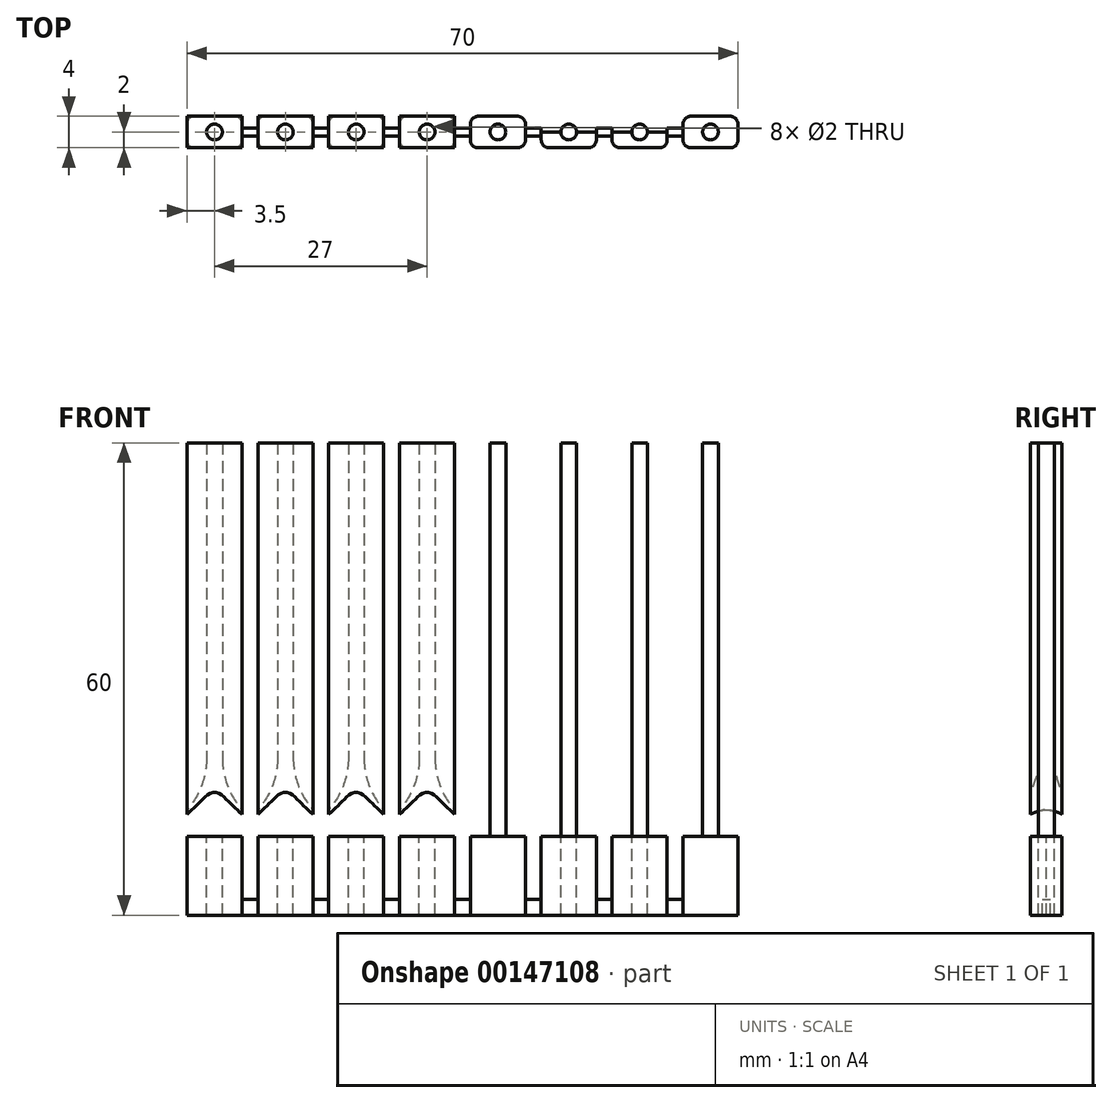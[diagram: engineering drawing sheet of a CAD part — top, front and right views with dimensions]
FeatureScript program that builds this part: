
annotation { "Feature Type Name" : "Feature", "Feature Type Description" : "" }
export const myFeature = defineFeature(function(context is Context, id is Id, definition is map)
    precondition{}
    {
        {
            var Q0;
            Q0=qCreatedBy(makeId("Top.planeOp"),FACE);
            var sketch = newSketch(context, id + "F0", { "sketchPlane" : qUnion([Q0])});
            skLineSegment(sketch, "E0.bottom", {"start": v(35, 2) * mm, "end": v(-35, 2) * mm});
            skLineSegment(sketch, "E0.top", {"start": v(35, -2) * mm, "end": v(-35, -2) * mm});
            skLineSegment(sketch, "E0.left", {"start": v(35, 2) * mm, "end": v(35, -2) * mm});
            skLineSegment(sketch, "E0.right", {"start": v(-35, 2) * mm, "end": v(-35, -2) * mm});
            skPoint(sketch, "E0.middle", {"position": v(0, 0) * mm});
            skLineSegment(sketch, "E1", {"start": v(0, 0) * mm, "end": v(4.5, 0) * mm});
            skLineSegment(sketch, "E2", {"start": v(4.5, 0) * mm, "end": v(13.5, 0) * mm});
            skLineSegment(sketch, "E3", {"start": v(13.5, 0) * mm, "end": v(22.5, 0) * mm});
            skLineSegment(sketch, "E4", {"start": v(22.5, 0) * mm, "end": v(31.5, 0) * mm});
            skCircle(sketch, "E5", {"center": v(4.5, 0) * mm, "radius": 1 * mm});
            skCircle(sketch, "E6", {"center": v(13.5, 0) * mm, "radius": 1 * mm});
            skCircle(sketch, "E7", {"center": v(22.5, 0) * mm, "radius": 1 * mm});
            skCircle(sketch, "E8", {"center": v(31.5, 0) * mm, "radius": 1 * mm});
            skLineSegment(sketch, "E9", {"start": v(0, 2) * mm, "end": v(8, 2) * mm});
            skLineSegment(sketch, "E10", {"start": v(8, 2) * mm, "end": v(10, 2) * mm});
            skLineSegment(sketch, "E11", {"start": v(10, 2) * mm, "end": v(17, 2) * mm});
            skLineSegment(sketch, "E12", {"start": v(17, 2) * mm, "end": v(19, 2) * mm});
            skLineSegment(sketch, "E13", {"start": v(19, 2) * mm, "end": v(26, 2) * mm});
            skLineSegment(sketch, "E14", {"start": v(26, 2) * mm, "end": v(28, 2) * mm});
            skLineSegment(sketch, "E15", {"start": v(8, 2) * mm, "end": v(8, 0.5) * mm});
            skLineSegment(sketch, "E16", {"start": v(8, 0.5) * mm, "end": v(10, 0.5) * mm});
            skLineSegment(sketch, "E17", {"start": v(10, 0.5) * mm, "end": v(10, 2) * mm});
            skLineSegment(sketch, "E18", {"start": v(17, 2) * mm, "end": v(17, 0.5) * mm});
            skLineSegment(sketch, "E19", {"start": v(17, 0.5) * mm, "end": v(19, 0.5) * mm});
            skLineSegment(sketch, "E20", {"start": v(19, 0.5) * mm, "end": v(19, 2) * mm});
            skLineSegment(sketch, "E21", {"start": v(26, 2) * mm, "end": v(26, 0.5) * mm});
            skLineSegment(sketch, "E22", {"start": v(26, 0.5) * mm, "end": v(28, 0.5) * mm});
            skLineSegment(sketch, "E23", {"start": v(28, 0.5) * mm, "end": v(28, 2) * mm});
            skLineSegment(sketch, "E24.MirrorCS", {"start": v(8, -0.5) * mm, "end": v(10, -0.5) * mm});
            skLineSegment(sketch, "E25.MirrorCS", {"start": v(8, -2) * mm, "end": v(8, -0.5) * mm});
            skLineSegment(sketch, "E26.MirrorCS", {"start": v(10, -0.5) * mm, "end": v(10, -2) * mm});
            skLineSegment(sketch, "E27.MirrorCS", {"start": v(17, -2) * mm, "end": v(17, -0.5) * mm});
            skLineSegment(sketch, "E28.MirrorCS", {"start": v(19, -0.5) * mm, "end": v(19, -2) * mm});
            skLineSegment(sketch, "E29.MirrorCS", {"start": v(17, -0.5) * mm, "end": v(19, -0.5) * mm});
            skLineSegment(sketch, "E30.MirrorCS", {"start": v(26, -0.5) * mm, "end": v(28, -0.5) * mm});
            skLineSegment(sketch, "E31.MirrorCS", {"start": v(28, -0.5) * mm, "end": v(28, -2) * mm});
            skLineSegment(sketch, "E32.MirrorCS", {"start": v(26, -2) * mm, "end": v(26, -0.5) * mm});
            skLineSegment(sketch, "E33", {"start": v(10, -0.5) * mm, "end": v(10, 0.5) * mm});
            skLineSegment(sketch, "E34", {"start": v(8, -0.5) * mm, "end": v(8, 0.5) * mm});
            skLineSegment(sketch, "E35", {"start": v(17, -0.5) * mm, "end": v(17, 0.5) * mm});
            skLineSegment(sketch, "E36", {"start": v(19, -0.5) * mm, "end": v(19, 0.5) * mm});
            skLineSegment(sketch, "E37", {"start": v(26, -0.5) * mm, "end": v(26, 0.5) * mm});
            skLineSegment(sketch, "E38", {"start": v(28, -0.5) * mm, "end": v(28, 0.5) * mm});
            skLineSegment(sketch, "E39.MirrorCS", {"start": v(-8, -2) * mm, "end": v(-8, -0.5) * mm});
            skCircle(sketch, "E40.MirrorC", {"center": v(-4.5, 0) * mm, "radius": 1 * mm});
            skLineSegment(sketch, "E41.MirrorCS", {"start": v(-8, 2) * mm, "end": v(-8, 0.5) * mm});
            skLineSegment(sketch, "E42.MirrorCS", {"start": v(-8, 0.5) * mm, "end": v(-10, 0.5) * mm});
            skLineSegment(sketch, "E43.MirrorCS", {"start": v(-10, -0.5) * mm, "end": v(-10, -2) * mm});
            skCircle(sketch, "E44.MirrorC", {"center": v(-13.5, 0) * mm, "radius": 1 * mm});
            skLineSegment(sketch, "E45.MirrorCS", {"start": v(-17, -2) * mm, "end": v(-17, -0.5) * mm});
            skLineSegment(sketch, "E46.MirrorCS", {"start": v(-19, -0.5) * mm, "end": v(-19, -2) * mm});
            skLineSegment(sketch, "E47.MirrorCS", {"start": v(-17, -0.5) * mm, "end": v(-19, -0.5) * mm});
            skLineSegment(sketch, "E48.MirrorCS", {"start": v(-17, 0.5) * mm, "end": v(-19, 0.5) * mm});
            skLineSegment(sketch, "E49.MirrorCS", {"start": v(-19, 0.5) * mm, "end": v(-19, 2) * mm});
            skLineSegment(sketch, "E50.MirrorCS", {"start": v(-17, 2) * mm, "end": v(-17, 0.5) * mm});
            skCircle(sketch, "E51.MirrorC", {"center": v(-22.5, 0) * mm, "radius": 1 * mm});
            skLineSegment(sketch, "E52.MirrorCS", {"start": v(-26, -2) * mm, "end": v(-26, -0.5) * mm});
            skLineSegment(sketch, "E53.MirrorCS", {"start": v(-28, -0.5) * mm, "end": v(-28, -2) * mm});
            skLineSegment(sketch, "E54.MirrorCS", {"start": v(-26, -0.5) * mm, "end": v(-28, -0.5) * mm});
            skLineSegment(sketch, "E55.MirrorCS", {"start": v(-26, 0.5) * mm, "end": v(-28, 0.5) * mm});
            skLineSegment(sketch, "E56.MirrorCS", {"start": v(-28, 0.5) * mm, "end": v(-28, 2) * mm});
            skLineSegment(sketch, "E57.MirrorCS", {"start": v(-26, 2) * mm, "end": v(-26, 0.5) * mm});
            skCircle(sketch, "E58.MirrorC", {"center": v(-31.5, 0) * mm, "radius": 1 * mm});
            skLineSegment(sketch, "E59.MirrorCS", {"start": v(-28, -0.5) * mm, "end": v(-28, 0.5) * mm});
            skLineSegment(sketch, "E60.MirrorCS", {"start": v(-26, -0.5) * mm, "end": v(-26, 0.5) * mm});
            skLineSegment(sketch, "E61.MirrorCS", {"start": v(-19, -0.5) * mm, "end": v(-19, 0.5) * mm});
            skLineSegment(sketch, "E62.MirrorCS", {"start": v(-17, -0.5) * mm, "end": v(-17, 0.5) * mm});
            skLineSegment(sketch, "E63.MirrorCS", {"start": v(-8, -0.5) * mm, "end": v(-8, 0.5) * mm});
            skLineSegment(sketch, "E64.MirrorCS", {"start": v(-10, -0.5) * mm, "end": v(-10, 0.5) * mm});
            skLineSegment(sketch, "E65.MirrorCS", {"start": v(-8, -0.5) * mm, "end": v(-10, -0.5) * mm});
            skLineSegment(sketch, "E66.MirrorCS", {"start": v(-10, 0.5) * mm, "end": v(-10, 2) * mm});
            skLineSegment(sketch, "E67", {"start": v(8, 2) * mm, "end": v(1, 2) * mm});
            skLineSegment(sketch, "E68", {"start": v(1, 2) * mm, "end": v(1, 0.5) * mm});
            skLineSegment(sketch, "E69", {"start": v(1, 0.5) * mm, "end": v(-1, 0.5) * mm});
            skLineSegment(sketch, "E70", {"start": v(-1, 0.5) * mm, "end": v(-1, 2) * mm});
            skLineSegment(sketch, "E71", {"start": v(8, -2) * mm, "end": v(1, -2) * mm});
            skLineSegment(sketch, "E72", {"start": v(1, -2) * mm, "end": v(1, -0.5) * mm});
            skLineSegment(sketch, "E73", {"start": v(1, -0.5) * mm, "end": v(-1, -0.5) * mm});
            skLineSegment(sketch, "E74", {"start": v(-1, -0.5) * mm, "end": v(-1, -2) * mm});
            skLineSegment(sketch, "E75", {"start": v(1, -0.5) * mm, "end": v(1, 0.5) * mm});
            skLineSegment(sketch, "E76", {"start": v(-1, -0.5) * mm, "end": v(-1, 0.5) * mm});
            skSolve(sketch);
        }
        {
            var Q0;
            {var subQ0=sQuery(id+"F0.wireOp",EDGE,"E0.left");Q0=makeQuery(id+"F0.imprint","IMPRINT",FACE,{"disambiguationData":[TD([[makeQuery(id+"F0.imprint","IMPRINT",EDGE,{"derivedFrom":subQ0}),-1.0]])]});}
            var Q1;
            {var subQ6=sQuery(id+"F0.wireOp",EDGE,"E0.right");Q1=makeQuery(id+"F0.imprint","IMPRINT",FACE,{"disambiguationData":[TD([[makeQuery(id+"F0.imprint","IMPRINT",EDGE,{"derivedFrom":subQ6}),1.0]])]});}
            var Q2;
            {var subQ10=sQuery(id+"F0.wireOp",EDGE,"E28.MirrorCS");Q2=makeQuery(id+"F0.imprint","IMPRINT",FACE,{"disambiguationData":[TD([[makeQuery(id+"F0.imprint","IMPRINT",EDGE,{"derivedFrom":subQ10}),1.0]])]});}
            var Q3;
            {var subQ5=sQuery(id+"F0.wireOp",EDGE,"E26.MirrorCS");Q3=makeQuery(id+"F0.imprint","IMPRINT",FACE,{"disambiguationData":[TD([[makeQuery(id+"F0.imprint","IMPRINT",EDGE,{"derivedFrom":subQ5}),1.0]])]});}
            var Q4;
            Q4=makeQuery(id+"F0.imprint","IMPRINT",FACE,{"disambiguationData":[TD([[makeQuery(id+"F0.imprint","IMPRINT",EDGE,{"derivedFrom":sQuery(id+"F0.wireOp",EDGE,"E11")}),-1.0]])]});
            var Q5;
            Q5=makeQuery(id+"F0.imprint","IMPRINT",FACE,{"disambiguationData":[TD([[makeQuery(id+"F0.imprint","IMPRINT",EDGE,{"derivedFrom":sQuery(id+"F0.wireOp",EDGE,"E13")}),-1.0]])]});
            var Q6;
            {var subQ1=sQuery(id+"F0.wireOp",EDGE,"E46.MirrorCS");Q6=makeQuery(id+"F0.imprint","IMPRINT",FACE,{"disambiguationData":[TD([[makeQuery(id+"F0.imprint","IMPRINT",EDGE,{"derivedFrom":subQ1}),-1.0]])]});}
            var Q7;
            {var subQ0=sQuery(id+"F0.wireOp",EDGE,"E43.MirrorCS");Q7=makeQuery(id+"F0.imprint","IMPRINT",FACE,{"disambiguationData":[TD([[makeQuery(id+"F0.imprint","IMPRINT",EDGE,{"derivedFrom":subQ0}),-1.0]])]});}
            var Q8;
            {var subQ2=sQuery(id+"F0.wireOp",EDGE,"E15");Q8=makeQuery(id+"F0.imprint","IMPRINT",FACE,{"disambiguationData":[TD([[makeQuery(id+"F0.imprint","IMPRINT",EDGE,{"derivedFrom":subQ2}),-1.0]])]});}
            var Q9;
            {var subQ0=sQuery(id+"F0.wireOp",EDGE,"E25.MirrorCS");Q9=makeQuery(id+"F0.imprint","IMPRINT",FACE,{"disambiguationData":[TD([[makeQuery(id+"F0.imprint","IMPRINT",EDGE,{"derivedFrom":subQ0}),1.0]])]});}
            var Q10;
            {var subQ0=sQuery(id+"F0.wireOp",EDGE,"E39.MirrorCS");Q10=makeQuery(id+"F0.imprint","IMPRINT",FACE,{"disambiguationData":[TD([[makeQuery(id+"F0.imprint","IMPRINT",EDGE,{"derivedFrom":subQ0}),-1.0]])]});}
            var Q11;
            Q11=makeQuery(id+"F0.imprint","IMPRINT",FACE,{"disambiguationData":[TD([[makeQuery(id+"F0.imprint","IMPRINT",EDGE,{"derivedFrom":sQuery(id+"F0.wireOp",EDGE,"E8")}),1.0]])]});
            var Q12;
            {var subQ0=sQuery(id+"F0.wireOp",EDGE,"E4");var subQ1=sQuery(id+"F0.wireOp",EDGE,"E3");var subQ2=makeQuery(id+"F0.imprint","INTERSECT",VERTEX,{"derivedFrom":[subQ1,subQ0]});Q12=makeQuery(id+"F0.imprint","IMPRINT",FACE,{"disambiguationData":[TD([[makeQuery(id+"F0.imprint","IMPRINT",EDGE,{"disambiguationData":[TD([[subQ2,1.0]])],"derivedFrom":subQ1}),1.0]])]});}
            var Q13;
            {var subQ0=sQuery(id+"F0.wireOp",EDGE,"E3");var subQ1=sQuery(id+"F0.wireOp",EDGE,"E2");var subQ2=makeQuery(id+"F0.imprint","INTERSECT",VERTEX,{"derivedFrom":[subQ1,subQ0]});Q13=makeQuery(id+"F0.imprint","IMPRINT",FACE,{"disambiguationData":[TD([[makeQuery(id+"F0.imprint","IMPRINT",EDGE,{"disambiguationData":[TD([[subQ2,1.0]])],"derivedFrom":subQ1}),1.0]])]});}
            var Q14;
            {var subQ0=sQuery(id+"F0.wireOp",EDGE,"E3");var subQ1=sQuery(id+"F0.wireOp",EDGE,"E2");var subQ2=makeQuery(id+"F0.imprint","INTERSECT",VERTEX,{"derivedFrom":[subQ1,subQ0]});Q14=makeQuery(id+"F0.imprint","IMPRINT",FACE,{"disambiguationData":[TD([[makeQuery(id+"F0.imprint","IMPRINT",EDGE,{"disambiguationData":[TD([[subQ2,1.0]])],"derivedFrom":subQ1}),-1.0]])]});}
            var Q15;
            {var subQ0=sQuery(id+"F0.wireOp",EDGE,"E4");var subQ1=sQuery(id+"F0.wireOp",EDGE,"E3");var subQ2=makeQuery(id+"F0.imprint","INTERSECT",VERTEX,{"derivedFrom":[subQ1,subQ0]});Q15=makeQuery(id+"F0.imprint","IMPRINT",FACE,{"disambiguationData":[TD([[makeQuery(id+"F0.imprint","IMPRINT",EDGE,{"disambiguationData":[TD([[subQ2,1.0]])],"derivedFrom":subQ1}),-1.0]])]});}
            var Q16;
            {var subQ0=sQuery(id+"F0.wireOp",EDGE,"E2");var subQ1=sQuery(id+"F0.wireOp",EDGE,"E1");var subQ2=makeQuery(id+"F0.imprint","INTERSECT",VERTEX,{"derivedFrom":[subQ1,subQ0]});Q16=makeQuery(id+"F0.imprint","IMPRINT",FACE,{"disambiguationData":[TD([[makeQuery(id+"F0.imprint","IMPRINT",EDGE,{"disambiguationData":[TD([[subQ2,1.0]])],"derivedFrom":subQ1}),1.0]])]});}
            var Q17;
            {var subQ0=sQuery(id+"F0.wireOp",EDGE,"E2");var subQ1=sQuery(id+"F0.wireOp",EDGE,"E1");var subQ2=makeQuery(id+"F0.imprint","INTERSECT",VERTEX,{"derivedFrom":[subQ1,subQ0]});Q17=makeQuery(id+"F0.imprint","IMPRINT",FACE,{"disambiguationData":[TD([[makeQuery(id+"F0.imprint","IMPRINT",EDGE,{"disambiguationData":[TD([[subQ2,1.0]])],"derivedFrom":subQ1}),-1.0]])]});}
            var Q18;
            Q18=makeQuery(id+"F0.imprint","IMPRINT",FACE,{"disambiguationData":[TD([[makeQuery(id+"F0.imprint","IMPRINT",EDGE,{"derivedFrom":sQuery(id+"F0.wireOp",EDGE,"E40.MirrorC")}),-1.0]])]});
            var Q19;
            Q19=makeQuery(id+"F0.imprint","IMPRINT",FACE,{"disambiguationData":[TD([[makeQuery(id+"F0.imprint","IMPRINT",EDGE,{"derivedFrom":sQuery(id+"F0.wireOp",EDGE,"E44.MirrorC")}),-1.0]])]});
            var Q20;
            Q20=makeQuery(id+"F0.imprint","IMPRINT",FACE,{"disambiguationData":[TD([[makeQuery(id+"F0.imprint","IMPRINT",EDGE,{"derivedFrom":sQuery(id+"F0.wireOp",EDGE,"E51.MirrorC")}),-1.0]])]});
            var Q21;
            Q21=makeQuery(id+"F0.imprint","IMPRINT",FACE,{"disambiguationData":[TD([[makeQuery(id+"F0.imprint","IMPRINT",EDGE,{"derivedFrom":sQuery(id+"F0.wireOp",EDGE,"E58.MirrorC")}),-1.0]])]});
            extrude(context, id + "F1", {"entities" : qUnion([Q0, Q1, Q2, Q3, Q4, Q5, Q6, Q7, Q8, Q9, Q10, Q11, Q12, Q13, Q14, Q15, Q16, Q17, Q18, Q19, Q20, Q21]), "oppositeDirection" : true, "depth" : 10 * mm});
        }
        {
            var Q0;
            {var subQ5=sQuery(id+"F0.wireOp",EDGE,"E24.MirrorCS");Q0=makeQuery(id+"F0.imprint","IMPRINT",FACE,{"disambiguationData":[TD([[makeQuery(id+"F0.imprint","IMPRINT",EDGE,{"derivedFrom":subQ5}),1.0]])]});}
            var Q1;
            {var subQ5=sQuery(id+"F0.wireOp",EDGE,"E16");Q1=makeQuery(id+"F0.imprint","IMPRINT",FACE,{"disambiguationData":[TD([[makeQuery(id+"F0.imprint","IMPRINT",EDGE,{"derivedFrom":subQ5}),-1.0]])]});}
            var Q2;
            {var subQ5=sQuery(id+"F0.wireOp",EDGE,"E29.MirrorCS");Q2=makeQuery(id+"F0.imprint","IMPRINT",FACE,{"disambiguationData":[TD([[makeQuery(id+"F0.imprint","IMPRINT",EDGE,{"derivedFrom":subQ5}),1.0]])]});}
            var Q3;
            {var subQ5=sQuery(id+"F0.wireOp",EDGE,"E19");Q3=makeQuery(id+"F0.imprint","IMPRINT",FACE,{"disambiguationData":[TD([[makeQuery(id+"F0.imprint","IMPRINT",EDGE,{"derivedFrom":subQ5}),-1.0]])]});}
            var Q4;
            {var subQ5=sQuery(id+"F0.wireOp",EDGE,"E30.MirrorCS");Q4=makeQuery(id+"F0.imprint","IMPRINT",FACE,{"disambiguationData":[TD([[makeQuery(id+"F0.imprint","IMPRINT",EDGE,{"derivedFrom":subQ5}),1.0]])]});}
            var Q5;
            {var subQ5=sQuery(id+"F0.wireOp",EDGE,"E22");Q5=makeQuery(id+"F0.imprint","IMPRINT",FACE,{"disambiguationData":[TD([[makeQuery(id+"F0.imprint","IMPRINT",EDGE,{"derivedFrom":subQ5}),-1.0]])]});}
            var Q6;
            {var subQ1=sQuery(id+"F0.wireOp",EDGE,"E69");Q6=makeQuery(id+"F0.imprint","IMPRINT",FACE,{"disambiguationData":[TD([[makeQuery(id+"F0.imprint","IMPRINT",EDGE,{"derivedFrom":subQ1}),1.0]])]});}
            var Q7;
            Q7=makeQuery(id+"F0.imprint","IMPRINT",FACE,{"disambiguationData":[TD([[makeQuery(id+"F0.imprint","IMPRINT",EDGE,{"derivedFrom":sQuery(id+"F0.wireOp",EDGE,"E42.MirrorCS")}),1.0]])]});
            var Q8;
            Q8=makeQuery(id+"F0.imprint","IMPRINT",FACE,{"disambiguationData":[TD([[makeQuery(id+"F0.imprint","IMPRINT",EDGE,{"derivedFrom":sQuery(id+"F0.wireOp",EDGE,"E47.MirrorCS")}),-1.0]])]});
            var Q9;
            Q9=makeQuery(id+"F0.imprint","IMPRINT",FACE,{"disambiguationData":[TD([[makeQuery(id+"F0.imprint","IMPRINT",EDGE,{"derivedFrom":sQuery(id+"F0.wireOp",EDGE,"E54.MirrorCS")}),-1.0]])]});
            extrude(context, id + "F2", {"entities" : qUnion([Q0, Q1, Q2, Q3, Q4, Q5, Q6, Q7, Q8, Q9]), "oppositeDirection" : true, "depth" : 10 * mm, "hasSecondDirection" : true, "secondDirectionOppositeDirection" : true, "secondDirectionDepth" : 8 * mm});
        }
        {
            var Q0;
            {var subQ0=sQuery(id+"F0.wireOp",EDGE,"E2");var subQ1=sQuery(id+"F0.wireOp",EDGE,"E1");var subQ2=makeQuery(id+"F0.imprint","INTERSECT",VERTEX,{"derivedFrom":[subQ1,subQ0]});Q0=makeQuery(id+"F0.imprint","IMPRINT",FACE,{"disambiguationData":[TD([[makeQuery(id+"F0.imprint","IMPRINT",EDGE,{"disambiguationData":[TD([[subQ2,1.0]])],"derivedFrom":subQ1}),-1.0]])]});}
            var Q1;
            {var subQ0=sQuery(id+"F0.wireOp",EDGE,"E3");var subQ1=sQuery(id+"F0.wireOp",EDGE,"E2");var subQ2=makeQuery(id+"F0.imprint","INTERSECT",VERTEX,{"derivedFrom":[subQ1,subQ0]});Q1=makeQuery(id+"F0.imprint","IMPRINT",FACE,{"disambiguationData":[TD([[makeQuery(id+"F0.imprint","IMPRINT",EDGE,{"disambiguationData":[TD([[subQ2,1.0]])],"derivedFrom":subQ1}),-1.0]])]});}
            var Q2;
            {var subQ0=sQuery(id+"F0.wireOp",EDGE,"E4");var subQ1=sQuery(id+"F0.wireOp",EDGE,"E3");var subQ2=makeQuery(id+"F0.imprint","INTERSECT",VERTEX,{"derivedFrom":[subQ1,subQ0]});Q2=makeQuery(id+"F0.imprint","IMPRINT",FACE,{"disambiguationData":[TD([[makeQuery(id+"F0.imprint","IMPRINT",EDGE,{"disambiguationData":[TD([[subQ2,1.0]])],"derivedFrom":subQ1}),-1.0]])]});}
            var Q3;
            Q3=makeQuery(id+"F0.imprint","IMPRINT",FACE,{"disambiguationData":[TD([[makeQuery(id+"F0.imprint","IMPRINT",EDGE,{"derivedFrom":sQuery(id+"F0.wireOp",EDGE,"E8")}),1.0]])]});
            var Q4;
            {var subQ0=sQuery(id+"F0.wireOp",EDGE,"E4");var subQ1=sQuery(id+"F0.wireOp",EDGE,"E3");var subQ2=makeQuery(id+"F0.imprint","INTERSECT",VERTEX,{"derivedFrom":[subQ1,subQ0]});Q4=makeQuery(id+"F0.imprint","IMPRINT",FACE,{"disambiguationData":[TD([[makeQuery(id+"F0.imprint","IMPRINT",EDGE,{"disambiguationData":[TD([[subQ2,1.0]])],"derivedFrom":subQ1}),1.0]])]});}
            var Q5;
            {var subQ0=sQuery(id+"F0.wireOp",EDGE,"E3");var subQ1=sQuery(id+"F0.wireOp",EDGE,"E2");var subQ2=makeQuery(id+"F0.imprint","INTERSECT",VERTEX,{"derivedFrom":[subQ1,subQ0]});Q5=makeQuery(id+"F0.imprint","IMPRINT",FACE,{"disambiguationData":[TD([[makeQuery(id+"F0.imprint","IMPRINT",EDGE,{"disambiguationData":[TD([[subQ2,1.0]])],"derivedFrom":subQ1}),1.0]])]});}
            var Q6;
            {var subQ0=sQuery(id+"F0.wireOp",EDGE,"E2");var subQ1=sQuery(id+"F0.wireOp",EDGE,"E1");var subQ2=makeQuery(id+"F0.imprint","INTERSECT",VERTEX,{"derivedFrom":[subQ1,subQ0]});Q6=makeQuery(id+"F0.imprint","IMPRINT",FACE,{"disambiguationData":[TD([[makeQuery(id+"F0.imprint","IMPRINT",EDGE,{"disambiguationData":[TD([[subQ2,1.0]])],"derivedFrom":subQ1}),1.0]])]});}
            var Q7;
            Q7=makeQuery(id+"F0.imprint","IMPRINT",FACE,{"disambiguationData":[TD([[makeQuery(id+"F0.imprint","IMPRINT",EDGE,{"derivedFrom":sQuery(id+"F0.wireOp",EDGE,"E40.MirrorC")}),-1.0]])]});
            var Q8;
            Q8=makeQuery(id+"F0.imprint","IMPRINT",FACE,{"disambiguationData":[TD([[makeQuery(id+"F0.imprint","IMPRINT",EDGE,{"derivedFrom":sQuery(id+"F0.wireOp",EDGE,"E44.MirrorC")}),-1.0]])]});
            var Q9;
            Q9=makeQuery(id+"F0.imprint","IMPRINT",FACE,{"disambiguationData":[TD([[makeQuery(id+"F0.imprint","IMPRINT",EDGE,{"derivedFrom":sQuery(id+"F0.wireOp",EDGE,"E51.MirrorC")}),-1.0]])]});
            var Q10;
            Q10=makeQuery(id+"F0.imprint","IMPRINT",FACE,{"disambiguationData":[TD([[makeQuery(id+"F0.imprint","IMPRINT",EDGE,{"derivedFrom":sQuery(id+"F0.wireOp",EDGE,"E58.MirrorC")}),-1.0]])]});
            extrude(context, id + "F3", {"entities" : qUnion([Q0, Q1, Q2, Q3, Q4, Q5, Q6, Q7, Q8, Q9, Q10]), "offsetDistance" : 25 * mm, "depth" : 50 * mm});
        }
        {
            var Q0;
            Q0=makeQuery(id+"F1.opExtrude","SWEPT_EDGE",EDGE,{"disambiguationData":[OSD([sQuery(id+"F0.wireOp",EDGE,"E0.bottom"),sQuery(id+"F0.wireOp",EDGE,"E0.left")])]});
            var Q1;
            Q1=makeQuery(id+"F1.opExtrude","SWEPT_EDGE",EDGE,{"disambiguationData":[OSD([sQuery(id+"F0.wireOp",EDGE,"E0.bottom"),sQuery(id+"F0.wireOp",EDGE,"E14"),sQuery(id+"F0.wireOp",EDGE,"E23")])]});
            var Q2;
            Q2=makeQuery(id+"F1.opExtrude","SWEPT_EDGE",EDGE,{"disambiguationData":[OSD([sQuery(id+"F0.wireOp",EDGE,"E0.top"),sQuery(id+"F0.wireOp",EDGE,"E0.left")])]});
            var Q3;
            Q3=makeQuery(id+"F1.opExtrude","SWEPT_EDGE",EDGE,{"disambiguationData":[OSD([sQuery(id+"F0.wireOp",EDGE,"E13"),sQuery(id+"F0.wireOp",EDGE,"E14"),sQuery(id+"F0.wireOp",EDGE,"E21")])]});
            var Q4;
            Q4=makeQuery(id+"F1.opExtrude","SWEPT_EDGE",EDGE,{"disambiguationData":[OSD([sQuery(id+"F0.wireOp",EDGE,"E12"),sQuery(id+"F0.wireOp",EDGE,"E13"),sQuery(id+"F0.wireOp",EDGE,"E20")])]});
            var Q5;
            Q5=makeQuery(id+"F1.opExtrude","SWEPT_EDGE",EDGE,{"disambiguationData":[OSD([sQuery(id+"F0.wireOp",EDGE,"E11"),sQuery(id+"F0.wireOp",EDGE,"E12"),sQuery(id+"F0.wireOp",EDGE,"E18")])]});
            var Q6;
            Q6=makeQuery(id+"F1.opExtrude","SWEPT_EDGE",EDGE,{"disambiguationData":[OSD([sQuery(id+"F0.wireOp",EDGE,"E10"),sQuery(id+"F0.wireOp",EDGE,"E11"),sQuery(id+"F0.wireOp",EDGE,"E17")])]});
            var Q7;
            Q7=makeQuery(id+"F1.opExtrude","SWEPT_EDGE",EDGE,{"disambiguationData":[OSD([sQuery(id+"F0.wireOp",EDGE,"E10"),sQuery(id+"F0.wireOp",EDGE,"E15"),sQuery(id+"F0.wireOp",EDGE,"E67")])]});
            var Q8;
            Q8=makeQuery(id+"F1.opExtrude","SWEPT_EDGE",EDGE,{"disambiguationData":[OSD([sQuery(id+"F0.wireOp",EDGE,"E9"),sQuery(id+"F0.wireOp",EDGE,"E67"),sQuery(id+"F0.wireOp",EDGE,"E68")])]});
            var Q9;
            Q9=makeQuery(id+"F1.opExtrude","SWEPT_EDGE",EDGE,{"disambiguationData":[OSD([sQuery(id+"F0.wireOp",EDGE,"E0.bottom"),sQuery(id+"F0.wireOp",EDGE,"E70")])]});
            var Q10;
            Q10=makeQuery(id+"F1.opExtrude","SWEPT_EDGE",EDGE,{"disambiguationData":[OSD([sQuery(id+"F0.wireOp",EDGE,"E0.bottom"),sQuery(id+"F0.wireOp",EDGE,"E41.MirrorCS")])]});
            var Q11;
            Q11=makeQuery(id+"F1.opExtrude","SWEPT_EDGE",EDGE,{"disambiguationData":[OSD([sQuery(id+"F0.wireOp",EDGE,"E0.bottom"),sQuery(id+"F0.wireOp",EDGE,"E66.MirrorCS")])]});
            var Q12;
            Q12=makeQuery(id+"F1.opExtrude","SWEPT_EDGE",EDGE,{"disambiguationData":[OSD([sQuery(id+"F0.wireOp",EDGE,"E0.bottom"),sQuery(id+"F0.wireOp",EDGE,"E50.MirrorCS")])]});
            var Q13;
            Q13=makeQuery(id+"F1.opExtrude","SWEPT_EDGE",EDGE,{"disambiguationData":[OSD([sQuery(id+"F0.wireOp",EDGE,"E0.bottom"),sQuery(id+"F0.wireOp",EDGE,"E49.MirrorCS")])]});
            var Q14;
            Q14=makeQuery(id+"F1.opExtrude","SWEPT_EDGE",EDGE,{"disambiguationData":[OSD([sQuery(id+"F0.wireOp",EDGE,"E0.bottom"),sQuery(id+"F0.wireOp",EDGE,"E57.MirrorCS")])]});
            var Q15;
            Q15=makeQuery(id+"F1.opExtrude","SWEPT_EDGE",EDGE,{"disambiguationData":[OSD([sQuery(id+"F0.wireOp",EDGE,"E0.bottom"),sQuery(id+"F0.wireOp",EDGE,"E56.MirrorCS")])]});
            var Q16;
            Q16=makeQuery(id+"F1.opExtrude","SWEPT_EDGE",EDGE,{"disambiguationData":[OSD([sQuery(id+"F0.wireOp",EDGE,"E0.bottom"),sQuery(id+"F0.wireOp",EDGE,"E0.right")])]});
            var Q17;
            Q17=makeQuery(id+"F1.opExtrude","SWEPT_EDGE",EDGE,{"disambiguationData":[OSD([sQuery(id+"F0.wireOp",EDGE,"E0.top"),sQuery(id+"F0.wireOp",EDGE,"E31.MirrorCS")])]});
            var Q18;
            Q18=makeQuery(id+"F1.opExtrude","SWEPT_EDGE",EDGE,{"disambiguationData":[OSD([sQuery(id+"F0.wireOp",EDGE,"E0.top"),sQuery(id+"F0.wireOp",EDGE,"E32.MirrorCS")])]});
            var Q19;
            Q19=makeQuery(id+"F1.opExtrude","SWEPT_EDGE",EDGE,{"disambiguationData":[OSD([sQuery(id+"F0.wireOp",EDGE,"E0.top"),sQuery(id+"F0.wireOp",EDGE,"E28.MirrorCS")])]});
            var Q20;
            Q20=makeQuery(id+"F1.opExtrude","SWEPT_EDGE",EDGE,{"disambiguationData":[OSD([sQuery(id+"F0.wireOp",EDGE,"E0.top"),sQuery(id+"F0.wireOp",EDGE,"E27.MirrorCS")])]});
            var Q21;
            Q21=makeQuery(id+"F1.opExtrude","SWEPT_EDGE",EDGE,{"disambiguationData":[OSD([sQuery(id+"F0.wireOp",EDGE,"E0.top"),sQuery(id+"F0.wireOp",EDGE,"E26.MirrorCS")])]});
            var Q22;
            Q22=makeQuery(id+"F1.opExtrude","SWEPT_EDGE",EDGE,{"disambiguationData":[OSD([sQuery(id+"F0.wireOp",EDGE,"E0.top"),sQuery(id+"F0.wireOp",EDGE,"E25.MirrorCS"),sQuery(id+"F0.wireOp",EDGE,"E71")])]});
            var Q23;
            Q23=makeQuery(id+"F1.opExtrude","SWEPT_EDGE",EDGE,{"disambiguationData":[OSD([sQuery(id+"F0.wireOp",EDGE,"E0.top"),sQuery(id+"F0.wireOp",EDGE,"E71"),sQuery(id+"F0.wireOp",EDGE,"E72")])]});
            var Q24;
            Q24=makeQuery(id+"F1.opExtrude","SWEPT_EDGE",EDGE,{"disambiguationData":[OSD([sQuery(id+"F0.wireOp",EDGE,"E0.top"),sQuery(id+"F0.wireOp",EDGE,"E74")])]});
            var Q25;
            Q25=makeQuery(id+"F1.opExtrude","SWEPT_EDGE",EDGE,{"disambiguationData":[OSD([sQuery(id+"F0.wireOp",EDGE,"E0.top"),sQuery(id+"F0.wireOp",EDGE,"E39.MirrorCS")])]});
            var Q26;
            Q26=makeQuery(id+"F1.opExtrude","SWEPT_EDGE",EDGE,{"disambiguationData":[OSD([sQuery(id+"F0.wireOp",EDGE,"E0.top"),sQuery(id+"F0.wireOp",EDGE,"E43.MirrorCS")])]});
            var Q27;
            Q27=makeQuery(id+"F1.opExtrude","SWEPT_EDGE",EDGE,{"disambiguationData":[OSD([sQuery(id+"F0.wireOp",EDGE,"E0.top"),sQuery(id+"F0.wireOp",EDGE,"E45.MirrorCS")])]});
            var Q28;
            Q28=makeQuery(id+"F1.opExtrude","SWEPT_EDGE",EDGE,{"disambiguationData":[OSD([sQuery(id+"F0.wireOp",EDGE,"E0.top"),sQuery(id+"F0.wireOp",EDGE,"E46.MirrorCS")])]});
            var Q29;
            Q29=makeQuery(id+"F1.opExtrude","SWEPT_EDGE",EDGE,{"disambiguationData":[OSD([sQuery(id+"F0.wireOp",EDGE,"E0.top"),sQuery(id+"F0.wireOp",EDGE,"E52.MirrorCS")])]});
            var Q30;
            Q30=makeQuery(id+"F1.opExtrude","SWEPT_EDGE",EDGE,{"disambiguationData":[OSD([sQuery(id+"F0.wireOp",EDGE,"E0.top"),sQuery(id+"F0.wireOp",EDGE,"E53.MirrorCS")])]});
            var Q31;
            Q31=makeQuery(id+"F1.opExtrude","SWEPT_EDGE",EDGE,{"disambiguationData":[OSD([sQuery(id+"F0.wireOp",EDGE,"E0.top"),sQuery(id+"F0.wireOp",EDGE,"E0.right")])]});
            fillet(context, id + "F4", {"entities" : qUnion([Q0, Q1, Q2, Q3, Q4, Q5, Q6, Q7, Q8, Q9, Q10, Q11, Q12, Q13, Q14, Q15, Q16, Q17, Q18, Q19, Q20, Q21, Q22, Q23, Q24, Q25, Q26, Q27, Q28, Q29, Q30, Q31]), "radius" : 1 * mm, "tangentPropagation" : true, "allowEdgeOverflow" : false});
        }
        {
            var Q0;
            Q0=makeQuery(id+"F3.opExtrude","CAP_EDGE",EDGE,{"disambiguationData":[OSD([sQuery(id+"F0.wireOp",EDGE,"E58.MirrorC")])],"isStart":true});
            var Q1;
            Q1=makeQuery(id+"F3.opExtrude","CAP_EDGE",EDGE,{"disambiguationData":[OSD([sQuery(id+"F0.wireOp",EDGE,"E51.MirrorC")])],"isStart":true});
            var Q2;
            Q2=makeQuery(id+"F3.opExtrude","CAP_EDGE",EDGE,{"disambiguationData":[OSD([sQuery(id+"F0.wireOp",EDGE,"E44.MirrorC")])],"isStart":true});
            var Q3;
            Q3=makeQuery(id+"F3.opExtrude","CAP_EDGE",EDGE,{"disambiguationData":[OSD([sQuery(id+"F0.wireOp",EDGE,"E40.MirrorC")])],"isStart":true});
            var Q4;
            Q4=makeQuery(id+"F3.opExtrude","CAP_EDGE",EDGE,{"disambiguationData":[OSD([sQuery(id+"F0.wireOp",EDGE,"E5")])],"isStart":true});
            var Q5;
            Q5=makeQuery(id+"F3.opExtrude","CAP_EDGE",EDGE,{"disambiguationData":[OSD([sQuery(id+"F0.wireOp",EDGE,"E6")])],"isStart":true});
            var Q6;
            Q6=makeQuery(id+"F3.opExtrude","CAP_EDGE",EDGE,{"disambiguationData":[OSD([sQuery(id+"F0.wireOp",EDGE,"E7")])],"isStart":true});
            var Q7;
            Q7=makeQuery(id+"F3.opExtrude","CAP_EDGE",EDGE,{"disambiguationData":[OSD([sQuery(id+"F0.wireOp",EDGE,"E8")])],"isStart":true});
            fillet(context, id + "F5", {"entities" : qUnion([Q0, Q1, Q2, Q3, Q4, Q5, Q6, Q7]), "tangentPropagation" : true, "radius" : 10 * mm, "defaultsChanged" : false, "vertexSettings" : [], "allowEdgeOverflow" : false});
        }
    });
